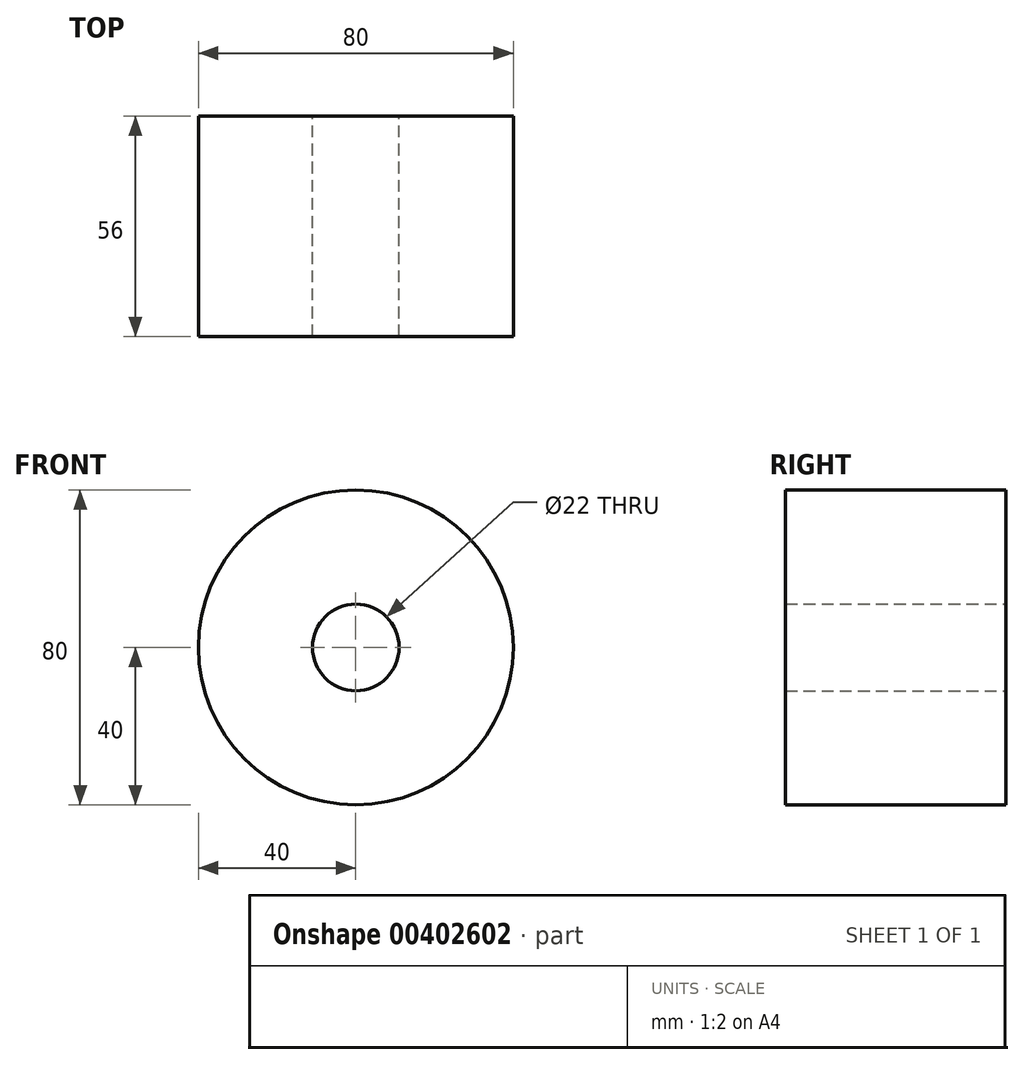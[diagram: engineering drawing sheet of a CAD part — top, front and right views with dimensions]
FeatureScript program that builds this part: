
annotation { "Feature Type Name" : "Feature", "Feature Type Description" : "" }
export const myFeature = defineFeature(function(context is Context, id is Id, definition is map)
    precondition{}
    {
        {
            var Q0;
            Q0=qCreatedBy(makeId("Front.planeOp"),FACE);
            var sketch = newSketch(context, id + "F0", { "sketchPlane" : qUnion([Q0])});
            skCircle(sketch, "E0", {"center": v(0, 0) * mm, "radius": 40 * mm});
            skCircle(sketch, "E1", {"center": v(0, 0) * mm, "radius": 11 * mm});
            skSolve(sketch);
        }
        {
            var Q0;
            Q0=makeQuery(id+"F0.imprint","IMPRINT",FACE,{"disambiguationData":[TD([[makeQuery(id+"F0.imprint","IMPRINT",EDGE,{"derivedFrom":sQuery(id+"F0.wireOp",EDGE,"E0")}),1.0]])]});
            extrude(context, id + "F1", {"entities" : qUnion([Q0]), "depth" : 56 * mm});
        }
    });
